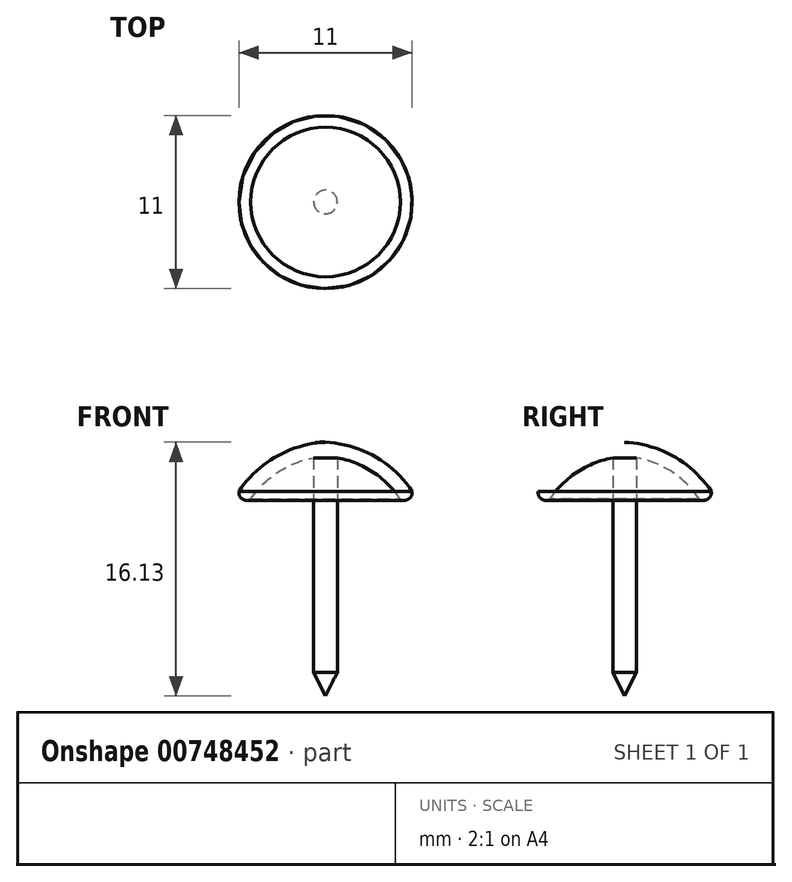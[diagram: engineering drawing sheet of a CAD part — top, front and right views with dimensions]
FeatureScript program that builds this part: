
annotation { "Feature Type Name" : "Feature", "Feature Type Description" : "" }
export const myFeature = defineFeature(function(context is Context, id is Id, definition is map)
    precondition{}
    {
        {
            var Q0;
            Q0=qCreatedBy(makeId("Front.planeOp"),FACE);
            var sketch = newSketch(context, id + "F0", { "sketchPlane" : qUnion([Q0])});
            skArc(sketch, "E0", {"start": v(0, 3.12) * mm, "mid": v(-3.12, 2.22) * mm, "end": v(-5.5, 0) * mm});
            skArc(sketch, "E1.0", {"start": v(0, 2.22) * mm, "mid": v(-2.7, 1.43) * mm, "end": v(-4.75, -0.5) * mm});
            skArc(sketch, "E2", {"start": v(-5.5, 0) * mm, "mid": v(-5.28, -0.48) * mm, "end": v(-4.75, -0.5) * mm});
            skLineSegment(sketch, "E3", {"start": v(0, -0.12) * mm, "end": v(0, 3.52) * mm});
            skSolve(sketch);
        }
        {
            var Q0;
            Q0=qCreatedBy(makeId("Front.planeOp"),FACE);
            var sketch = newSketch(context, id + "F1", { "sketchPlane" : qUnion([Q0])});
            skLineSegment(sketch, "E4", {"start": v(0, 0) * mm, "end": v(0, 6.71) * mm, "construction": true});
            skSolve(sketch);
        }
        {
            var Q0;
            {var subQ0=sQuery(id+"F0.wireOp",EDGE,"E0");Q0=makeQuery(id+"F0.imprint","IMPRINT",FACE,{"disambiguationData":[TD([[makeQuery(id+"F0.imprint","IMPRINT",EDGE,{"derivedFrom":subQ0}),1.0]])]});}
            var Q1;
            Q1=qConstructionFilter(qBodyType(qCreatedBy(id+"F0",EDGE),BodyType.WIRE),ConstructionObject.NO);
            var Q2;
            Q2=sQuery(id+"F1.wireOp",EDGE,"E4");
            revolve(context, id + "F2", {"entities" : qUnion([Q0]), "surfaceEntities" : qUnion([Q1]), "axis" : qUnion([Q2]), "revolveType" : RevolveType.FULL});
        }
        {
            var Q0;
            Q0=qCreatedBy(makeId("Front.planeOp"),FACE);
            var sketch = newSketch(context, id + "F3", { "sketchPlane" : qUnion([Q0])});
            skLineSegment(sketch, "E5", {"start": v(0, 3) * mm, "end": v(0, -13) * mm});
            skLineSegment(sketch, "E6.0", {"start": v(-0.75, 3) * mm, "end": v(-0.75, -11.5) * mm});
            skLineSegment(sketch, "E7", {"start": v(-0.75, -11.5) * mm, "end": v(0, -13) * mm});
            skLineSegment(sketch, "E8", {"start": v(0, -13) * mm, "end": v(0, -13) * mm});
            skLineSegment(sketch, "E9", {"start": v(-0.75, 3) * mm, "end": v(0, 3) * mm});
            skSolve(sketch);
        }
        {
            var Q0;
            Q0=makeQuery(id+"F3.imprint","IMPRINT",FACE,{"disambiguationData":[TD([[makeQuery(id+"F3.imprint","IMPRINT",EDGE,{"derivedFrom":sQuery(id+"F3.wireOp",EDGE,"E5")}),-1.0]])]});
            var Q1;
            Q1=sQuery(id+"F1.wireOp",EDGE,"E4");
            revolve(context, id + "F4", {"operationType" : NewBodyOperationType.ADD, "entities" : qUnion([Q0]), "axis" : qUnion([Q1]), "revolveType" : RevolveType.FULL});
        }
    });
